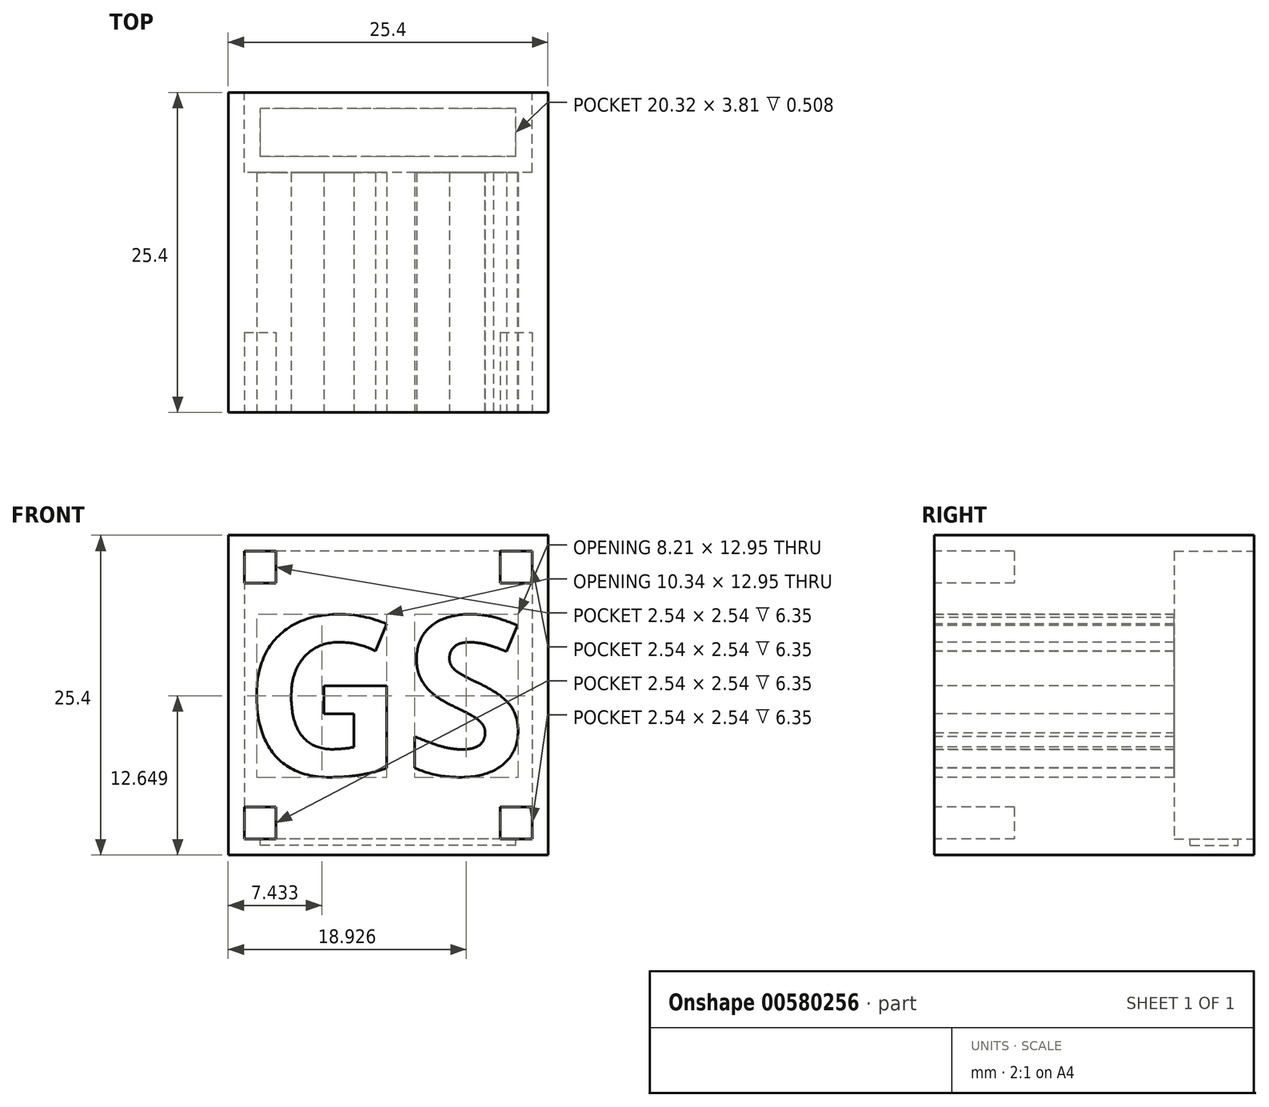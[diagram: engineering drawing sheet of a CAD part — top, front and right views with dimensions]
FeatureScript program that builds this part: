
annotation { "Feature Type Name" : "Feature", "Feature Type Description" : "" }
export const myFeature = defineFeature(function(context is Context, id is Id, definition is map)
    precondition{}
    {
        {
            var Q0;
            Q0=qCreatedBy(makeId("Front.planeOp"),FACE);
            var sketch = newSketch(context, id + "F0", { "sketchPlane" : qUnion([Q0])});
            skLineSegment(sketch, "E0.bottom", {"start": v(-10.9, 12.7) * mm, "end": v(14.5, 12.7) * mm});
            skLineSegment(sketch, "E0.top", {"start": v(-10.9, -12.7) * mm, "end": v(14.5, -12.7) * mm});
            skLineSegment(sketch, "E0.left", {"start": v(-10.9, 12.7) * mm, "end": v(-10.9, -12.7) * mm});
            skLineSegment(sketch, "E0.right", {"start": v(14.5, 12.7) * mm, "end": v(14.5, -12.7) * mm});
            skSolve(sketch);
        }
        {
            var Q0;
            Q0 = qSketchRegion(id + "F0", true);
            extrude(context, id + "F1", {"entities" : qUnion([Q0]), "depth" : 25.4 * mm, "offsetDistance" : 25.4 * mm});
        }
        {
            var Q0;
            Q0=makeQuery(id+"F1.opExtrude","CAP_FACE",FACE,{"disambiguationData":[OSD([sQuery(id+"F0.wireOp",EDGE,"E0.bottom"),sQuery(id+"F0.wireOp",EDGE,"E0.top"),sQuery(id+"F0.wireOp",EDGE,"E0.left"),sQuery(id+"F0.wireOp",EDGE,"E0.right")])],"isStart":false});
            var sketch = newSketch(context, id + "F2", { "sketchPlane" : qUnion([Q0])});
            skText(sketch, "E1", { "text": "GS", "fontName": "OpenSans-Bold.ttf"});
            const initialGuessF2  = {"E1": [-0.00966, -0.00635, 1, 0, 0.0127]};
            skSetInitialGuess(sketch, initialGuessF2);
            skSolve(sketch);
        }
        {
            var Q0;
            Q0 = qSketchRegion(id + "F2", true);
            extrude(context, id + "F3", {"entities" : qUnion([Q0]), "operationType" : NewBodyOperationType.REMOVE, "oppositeDirection" : true, "depth" : 19.05 * mm, "offsetDistance" : 25.4 * mm});
        }
        {
            var Q0;
            Q0=makeQuery(id+"F1.opExtrude","CAP_FACE",FACE,{"disambiguationData":[OSD([sQuery(id+"F0.wireOp",EDGE,"E0.bottom"),sQuery(id+"F0.wireOp",EDGE,"E0.top"),sQuery(id+"F0.wireOp",EDGE,"E0.left"),sQuery(id+"F0.wireOp",EDGE,"E0.right")])],"isStart":false});
            var sketch = newSketch(context, id + "F4", { "sketchPlane" : qUnion([Q0])});
            skLineSegment(sketch, "E2.bottom", {"start": v(-9.63, 11.43) * mm, "end": v(-7.09, 11.43) * mm});
            skLineSegment(sketch, "E2.top", {"start": v(-9.63, 8.9) * mm, "end": v(-7.09, 8.9) * mm});
            skLineSegment(sketch, "E2.left", {"start": v(-9.63, 11.43) * mm, "end": v(-9.63, 8.9) * mm});
            skLineSegment(sketch, "E2.right", {"start": v(-7.09, 11.43) * mm, "end": v(-7.09, 8.9) * mm});
            skSolve(sketch);
        }
        {
            var Q0;
            Q0 = qSketchRegion(id + "F4", true);
            extrude(context, id + "F5", {"entities" : qUnion([Q0]), "operationType" : NewBodyOperationType.REMOVE, "oppositeDirection" : true, "depth" : 6.35 * mm, "offsetDistance" : 25.4 * mm});
        }
        {
            var Q0;
            Q0=makeQuery(id+"F1.opExtrude","CAP_FACE",FACE,{"disambiguationData":[OSD([sQuery(id+"F0.wireOp",EDGE,"E0.bottom"),sQuery(id+"F0.wireOp",EDGE,"E0.top"),sQuery(id+"F0.wireOp",EDGE,"E0.left"),sQuery(id+"F0.wireOp",EDGE,"E0.right")])],"isStart":false});
            var sketch = newSketch(context, id + "F6", { "sketchPlane" : qUnion([Q0])});
            skLineSegment(sketch, "E3.bottom", {"start": v(10.7, 11.43) * mm, "end": v(13.23, 11.43) * mm});
            skLineSegment(sketch, "E3.top", {"start": v(10.7, 8.9) * mm, "end": v(13.23, 8.9) * mm});
            skLineSegment(sketch, "E3.left", {"start": v(10.7, 11.43) * mm, "end": v(10.7, 8.9) * mm});
            skLineSegment(sketch, "E3.right", {"start": v(13.23, 11.43) * mm, "end": v(13.23, 8.9) * mm});
            skSolve(sketch);
        }
        {
            var Q0;
            Q0 = qSketchRegion(id + "F6", true);
            extrude(context, id + "F7", {"entities" : qUnion([Q0]), "operationType" : NewBodyOperationType.REMOVE, "oppositeDirection" : true, "depth" : 6.35 * mm, "offsetDistance" : 25.4 * mm});
        }
        {
            var Q0;
            Q0=makeQuery(id+"F1.opExtrude","CAP_FACE",FACE,{"disambiguationData":[OSD([sQuery(id+"F0.wireOp",EDGE,"E0.bottom"),sQuery(id+"F0.wireOp",EDGE,"E0.top"),sQuery(id+"F0.wireOp",EDGE,"E0.left"),sQuery(id+"F0.wireOp",EDGE,"E0.right")])],"isStart":false});
            var sketch = newSketch(context, id + "F8", { "sketchPlane" : qUnion([Q0])});
            skLineSegment(sketch, "E4.bottom", {"start": v(-9.63, -8.9) * mm, "end": v(-7.09, -8.9) * mm});
            skLineSegment(sketch, "E4.top", {"start": v(-9.63, -11.43) * mm, "end": v(-7.09, -11.43) * mm});
            skLineSegment(sketch, "E4.left", {"start": v(-9.63, -8.9) * mm, "end": v(-9.63, -11.43) * mm});
            skLineSegment(sketch, "E4.right", {"start": v(-7.09, -8.9) * mm, "end": v(-7.09, -11.43) * mm});
            skSolve(sketch);
        }
        {
            var Q0;
            Q0 = qSketchRegion(id + "F8", true);
            extrude(context, id + "F9", {"entities" : qUnion([Q0]), "operationType" : NewBodyOperationType.REMOVE, "oppositeDirection" : true, "depth" : 6.35 * mm, "offsetDistance" : 25.4 * mm});
        }
        {
            var Q0;
            Q0=makeQuery(id+"F1.opExtrude","CAP_FACE",FACE,{"disambiguationData":[OSD([sQuery(id+"F0.wireOp",EDGE,"E0.bottom"),sQuery(id+"F0.wireOp",EDGE,"E0.top"),sQuery(id+"F0.wireOp",EDGE,"E0.left"),sQuery(id+"F0.wireOp",EDGE,"E0.right")])],"isStart":false});
            var sketch = newSketch(context, id + "F10", { "sketchPlane" : qUnion([Q0])});
            skLineSegment(sketch, "E5.bottom", {"start": v(13.23, -11.43) * mm, "end": v(10.7, -11.43) * mm});
            skLineSegment(sketch, "E5.top", {"start": v(13.23, -8.9) * mm, "end": v(10.7, -8.9) * mm});
            skLineSegment(sketch, "E5.left", {"start": v(13.23, -11.43) * mm, "end": v(13.23, -8.9) * mm});
            skLineSegment(sketch, "E5.right", {"start": v(10.7, -11.43) * mm, "end": v(10.7, -8.9) * mm});
            skSolve(sketch);
        }
        {
            var Q0;
            Q0 = qSketchRegion(id + "F10", true);
            extrude(context, id + "F11", {"entities" : qUnion([Q0]), "operationType" : NewBodyOperationType.REMOVE, "oppositeDirection" : true, "depth" : 6.35 * mm, "offsetDistance" : 25.4 * mm});
        }
        {
            var Q0;
            Q0=makeQuery(id+"F1.opExtrude","CAP_FACE",FACE,{"disambiguationData":[OSD([sQuery(id+"F0.wireOp",EDGE,"E0.bottom"),sQuery(id+"F0.wireOp",EDGE,"E0.top"),sQuery(id+"F0.wireOp",EDGE,"E0.left"),sQuery(id+"F0.wireOp",EDGE,"E0.right")])],"isStart":true});
            var sketch = newSketch(context, id + "F12", { "sketchPlane" : qUnion([Q0])});
            skLineSegment(sketch, "E6.bottom", {"start": v(-13.23, 11.43) * mm, "end": v(9.63, 11.43) * mm});
            skLineSegment(sketch, "E6.top", {"start": v(-13.23, -11.43) * mm, "end": v(9.63, -11.43) * mm});
            skLineSegment(sketch, "E6.left", {"start": v(-13.23, 11.43) * mm, "end": v(-13.23, -11.43) * mm});
            skLineSegment(sketch, "E6.right", {"start": v(9.63, 11.43) * mm, "end": v(9.63, -11.43) * mm});
            skSolve(sketch);
        }
        {
            var Q0;
            Q0 = qSketchRegion(id + "F12", true);
            extrude(context, id + "F13", {"entities" : qUnion([Q0]), "operationType" : NewBodyOperationType.REMOVE, "oppositeDirection" : true, "depth" : 6.35 * mm, "offsetDistance" : 25.4 * mm});
        }
        {
            var Q0;
            Q0=makeQuery(id+"F13.boolean.opBoolean","COPY",FACE,{"derivedFrom":makeQuery(id+"F13.opExtrude","SWEPT_FACE",FACE,{"disambiguationData":[OSD([sQuery(id+"F12.wireOp",EDGE,"E6.top")])]})});
            var sketch = newSketch(context, id + "F14", { "sketchPlane" : qUnion([Q0])});
            skLineSegment(sketch, "E7.bottom", {"start": v(11.96, -5.08) * mm, "end": v(-8.36, -5.08) * mm});
            skLineSegment(sketch, "E7.top", {"start": v(11.96, -1.27) * mm, "end": v(-8.36, -1.27) * mm});
            skLineSegment(sketch, "E7.left", {"start": v(11.96, -5.08) * mm, "end": v(11.96, -1.27) * mm});
            skLineSegment(sketch, "E7.right", {"start": v(-8.36, -5.08) * mm, "end": v(-8.36, -1.27) * mm});
            skSolve(sketch);
        }
        {
            var Q0;
            Q0 = qSketchRegion(id + "F14", true);
            extrude(context, id + "F15", {"entities" : qUnion([Q0]), "operationType" : NewBodyOperationType.REMOVE, "oppositeDirection" : true, "depth" : 0.5 * mm, "offsetDistance" : 25.4 * mm});
        }
    });
